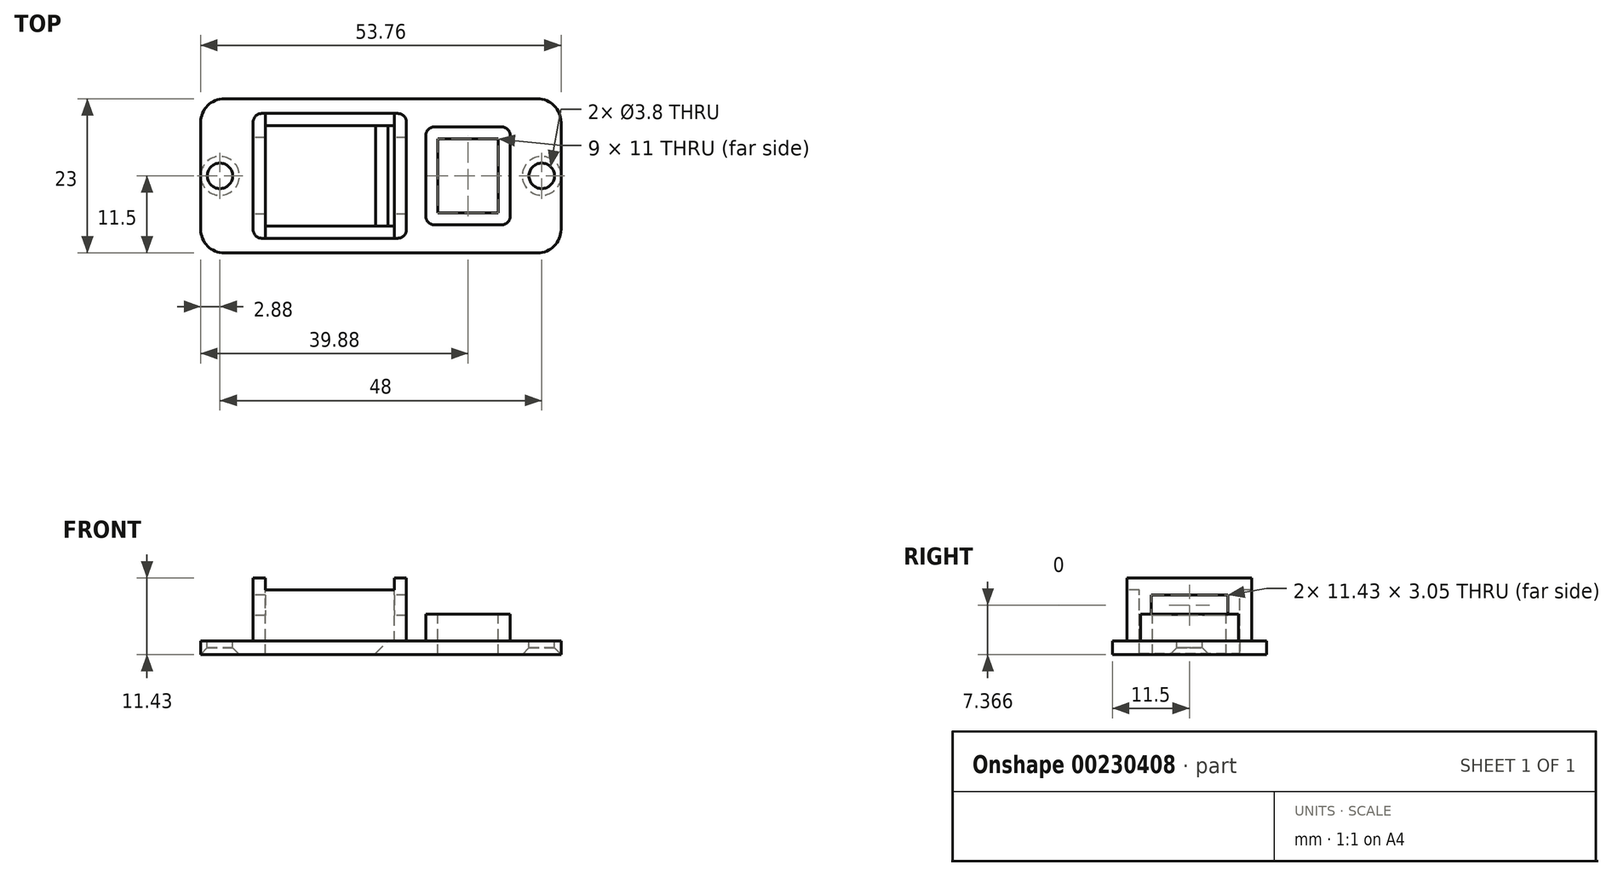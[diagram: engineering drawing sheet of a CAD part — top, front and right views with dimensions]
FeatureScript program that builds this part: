
annotation { "Feature Type Name" : "Feature", "Feature Type Description" : "" }
export const myFeature = defineFeature(function(context is Context, id is Id, definition is map)
    precondition{}
    {
        {
            var Q0;
            Q0=qCreatedBy(makeId("Top.planeOp"),FACE);
            var sketch = newSketch(context, id + "F0", { "sketchPlane" : qUnion([Q0])});
            skLineSegment(sketch, "E0.bottom", {"start": v(23.38, 11.5) * mm, "end": v(-23.38, 11.5) * mm});
            skLineSegment(sketch, "E0.top", {"start": v(23.37, -11.5) * mm, "end": v(-23.37, -11.5) * mm});
            skLineSegment(sketch, "E0.left", {"start": v(26.87, 8) * mm, "end": v(26.87, -8) * mm});
            skLineSegment(sketch, "E0.right", {"start": v(-26.88, 8) * mm, "end": v(-26.88, -8) * mm});
            skPoint(sketch, "E0.middle", {"position": v(0, 0) * mm});
            skPoint(sketch, "E1.visualSharp", {"position": v(-26.88, 11.5) * mm});
            skArc(sketch, "E1.filletArc", {"start": v(-23.38, 11.5) * mm, "mid": v(-25.85, 10.47) * mm, "end": v(-26.88, 8) * mm});
            skPoint(sketch, "E2.visualSharp", {"position": v(26.87, 11.5) * mm});
            skArc(sketch, "E2.filletArc", {"start": v(26.88, 8) * mm, "mid": v(25.85, 10.47) * mm, "end": v(23.38, 11.5) * mm});
            skPoint(sketch, "E3.visualSharp", {"position": v(26.87, -11.5) * mm});
            skArc(sketch, "E3.filletArc", {"start": v(23.38, -11.5) * mm, "mid": v(25.85, -10.47) * mm, "end": v(26.88, -8) * mm});
            skPoint(sketch, "E4.visualSharp", {"position": v(-26.87, -11.5) * mm});
            skArc(sketch, "E4.filletArc", {"start": v(-26.88, -8) * mm, "mid": v(-25.85, -10.47) * mm, "end": v(-23.38, -11.5) * mm});
            skSolve(sketch);
        }
        {
            var Q0;
            Q0=makeQuery(id+"F0.imprint","IMPRINT",FACE,{"disambiguationData":[TD([[makeQuery(id+"F0.imprint","IMPRINT",EDGE,{"derivedFrom":sQuery(id+"F0.wireOp",EDGE,"E0.bottom")}),1.0]])]});
            extrude(context, id + "F1", {"entities" : qUnion([Q0]), "depth" : 2 * mm});
        }
        {
            var Q0;
            Q0=makeQuery(id+"F1.opExtrude","CAP_FACE",FACE,{"disambiguationData":[OSD([sQuery(id+"F0.wireOp",EDGE,"E0.bottom"),sQuery(id+"F0.wireOp",EDGE,"E0.top"),sQuery(id+"F0.wireOp",EDGE,"E0.left"),sQuery(id+"F0.wireOp",EDGE,"E0.right"),sQuery(id+"F0.wireOp",EDGE,"E1.filletArc"),sQuery(id+"F0.wireOp",EDGE,"E2.filletArc"),sQuery(id+"F0.wireOp",EDGE,"E3.filletArc"),sQuery(id+"F0.wireOp",EDGE,"E4.filletArc")])],"isStart":false});
            var sketch = newSketch(context, id + "F2", { "sketchPlane" : qUnion([Q0])});
            skCircle(sketch, "E5", {"center": v(-24, 0) * mm, "radius": 1.9 * mm});
            skCircle(sketch, "E6", {"center": v(24, 0) * mm, "radius": 1.9 * mm});
            skSolve(sketch);
        }
        {
            var Q0;
            Q0 = qSketchRegion(id + "F2", true);
            extrude(context, id + "F3", {"entities" : qUnion([Q0]), "operationType" : NewBodyOperationType.REMOVE, "endBound" : BoundingType.THROUGH_ALL, "oppositeDirection" : true, "depth" : 25 * mm});
        }
        {
            var Q0;
            Q0=makeQuery(id+"F3.boolean.opBoolean","INTERSECT",EDGE,{"derivedFrom":[makeQuery(id+"F1.opExtrude","CAP_FACE",FACE,{"disambiguationData":[OSD([sQuery(id+"F0.wireOp",EDGE,"E0.bottom"),sQuery(id+"F0.wireOp",EDGE,"E0.top"),sQuery(id+"F0.wireOp",EDGE,"E0.left"),sQuery(id+"F0.wireOp",EDGE,"E0.right"),sQuery(id+"F0.wireOp",EDGE,"E1.filletArc"),sQuery(id+"F0.wireOp",EDGE,"E2.filletArc"),sQuery(id+"F0.wireOp",EDGE,"E3.filletArc"),sQuery(id+"F0.wireOp",EDGE,"E4.filletArc")])],"isStart":true}),makeQuery(id+"F3.opExtrude","SWEPT_FACE",FACE,{"disambiguationData":[OSD([sQuery(id+"F2.wireOp",EDGE,"E5")])]})]});
            var Q1;
            Q1=makeQuery(id+"F3.boolean.opBoolean","INTERSECT",EDGE,{"derivedFrom":[makeQuery(id+"F1.opExtrude","CAP_FACE",FACE,{"disambiguationData":[OSD([sQuery(id+"F0.wireOp",EDGE,"E0.bottom"),sQuery(id+"F0.wireOp",EDGE,"E0.top"),sQuery(id+"F0.wireOp",EDGE,"E0.left"),sQuery(id+"F0.wireOp",EDGE,"E0.right"),sQuery(id+"F0.wireOp",EDGE,"E1.filletArc"),sQuery(id+"F0.wireOp",EDGE,"E2.filletArc"),sQuery(id+"F0.wireOp",EDGE,"E3.filletArc"),sQuery(id+"F0.wireOp",EDGE,"E4.filletArc")])],"isStart":true}),makeQuery(id+"F3.opExtrude","SWEPT_FACE",FACE,{"disambiguationData":[OSD([sQuery(id+"F2.wireOp",EDGE,"E6")])]})]});
            chamfer(context, id + "F4", {"entities" : qUnion([Q0, Q1]), "width" : 1 * mm, "tangentPropagation" : true});
        }
        {
            var Q0;
            Q0=makeQuery(id+"F1.opExtrude","CAP_FACE",FACE,{"disambiguationData":[OSD([sQuery(id+"F0.wireOp",EDGE,"E0.bottom"),sQuery(id+"F0.wireOp",EDGE,"E0.top"),sQuery(id+"F0.wireOp",EDGE,"E0.left"),sQuery(id+"F0.wireOp",EDGE,"E0.right"),sQuery(id+"F0.wireOp",EDGE,"E1.filletArc"),sQuery(id+"F0.wireOp",EDGE,"E2.filletArc"),sQuery(id+"F0.wireOp",EDGE,"E3.filletArc"),sQuery(id+"F0.wireOp",EDGE,"E4.filletArc")])],"isStart":false});
            var sketch = newSketch(context, id + "F5", { "sketchPlane" : qUnion([Q0])});
            skLineSegment(sketch, "E7.bottom", {"start": v(2, -7.5) * mm, "end": v(-17.25, -7.5) * mm});
            skLineSegment(sketch, "E7.top", {"start": v(2, 7.5) * mm, "end": v(-17.25, 7.5) * mm});
            skLineSegment(sketch, "E7.left", {"start": v(2, -7.5) * mm, "end": v(2, 7.5) * mm});
            skLineSegment(sketch, "E7.right", {"start": v(-17.25, -7.5) * mm, "end": v(-17.25, 7.5) * mm});
            skPoint(sketch, "E7.middle", {"position": v(-7.63, 0) * mm});
            skSolve(sketch);
        }
        {
            var Q0;
            Q0 = qSketchRegion(id + "F5", true);
            extrude(context, id + "F6", {"entities" : qUnion([Q0]), "operationType" : NewBodyOperationType.REMOVE, "endBound" : BoundingType.THROUGH_ALL, "oppositeDirection" : true, "depth" : 25 * mm});
        }
        {
            var Q0;
            Q0=makeQuery(id+"F1.opExtrude","CAP_FACE",FACE,{"disambiguationData":[OSD([sQuery(id+"F0.wireOp",EDGE,"E0.bottom"),sQuery(id+"F0.wireOp",EDGE,"E0.top"),sQuery(id+"F0.wireOp",EDGE,"E0.left"),sQuery(id+"F0.wireOp",EDGE,"E0.right"),sQuery(id+"F0.wireOp",EDGE,"E1.filletArc"),sQuery(id+"F0.wireOp",EDGE,"E2.filletArc"),sQuery(id+"F0.wireOp",EDGE,"E3.filletArc"),sQuery(id+"F0.wireOp",EDGE,"E4.filletArc")])],"isStart":false});
            var sketch = newSketch(context, id + "F7", { "sketchPlane" : qUnion([Q0])});
            skLineSegment(sketch, "E8.0", {"start": v(2, 7.5) * mm, "end": v(-17.25, 7.5) * mm});
            skLineSegment(sketch, "E9.0", {"start": v(-17.25, -7.5) * mm, "end": v(-17.25, 7.5) * mm});
            skLineSegment(sketch, "E10.0", {"start": v(2, -7.5) * mm, "end": v(-17.25, -7.5) * mm});
            skLineSegment(sketch, "E11.0", {"start": v(2, -7.5) * mm, "end": v(2, 7.5) * mm});
            skLineSegment(sketch, "E12.0", {"start": v(2.53, 9.3) * mm, "end": v(-17.78, 9.3) * mm});
            skLineSegment(sketch, "E12.1", {"start": v(3.8, -8.04) * mm, "end": v(3.8, 8.04) * mm});
            skLineSegment(sketch, "E12.2", {"start": v(2.53, -9.3) * mm, "end": v(-17.78, -9.3) * mm});
            skLineSegment(sketch, "E12.3", {"start": v(-19.05, -8.04) * mm, "end": v(-19.05, 8.04) * mm});
            skPoint(sketch, "E13.visualSharp", {"position": v(-19.05, 9.3) * mm});
            skArc(sketch, "E13.filletArc", {"start": v(-17.78, 9.3) * mm, "mid": v(-18.68, 8.93) * mm, "end": v(-19.05, 8.04) * mm});
            skPoint(sketch, "E14.visualSharp", {"position": v(3.8, 9.3) * mm});
            skArc(sketch, "E14.filletArc", {"start": v(3.8, 8.04) * mm, "mid": v(3.43, 8.93) * mm, "end": v(2.53, 9.3) * mm});
            skPoint(sketch, "E15.visualSharp", {"position": v(3.8, -9.3) * mm});
            skArc(sketch, "E15.filletArc", {"start": v(2.53, -9.3) * mm, "mid": v(3.43, -8.93) * mm, "end": v(3.8, -8.04) * mm});
            skPoint(sketch, "E16.visualSharp", {"position": v(-19.05, -9.3) * mm});
            skArc(sketch, "E16.filletArc", {"start": v(-19.05, -8.04) * mm, "mid": v(-18.68, -8.93) * mm, "end": v(-17.78, -9.3) * mm});
            skSolve(sketch);
        }
        {
            var Q0;
            Q0 = qSketchRegion(id + "F7", true);
            extrude(context, id + "F8", {"entities" : qUnion([Q0]), "operationType" : NewBodyOperationType.ADD, "depth" : 11.43 * mm - 2 * mm});
        }
        {
            var Q0;
            Q0=makeQuery(id+"F8.opExtrude","SWEPT_FACE",FACE,{"disambiguationData":[OSD([sQuery(id+"F7.wireOp",EDGE,"E12.3")])]});
            var sketch = newSketch(context, id + "F9", { "sketchPlane" : qUnion([Q0])});
            skLineSegment(sketch, "E17.bottom", {"start": v(5.71, 5.84) * mm, "end": v(-5.72, 5.84) * mm});
            skLineSegment(sketch, "E17.top", {"start": v(5.71, 8.9) * mm, "end": v(-5.72, 8.9) * mm});
            skLineSegment(sketch, "E17.left", {"start": v(5.71, 5.84) * mm, "end": v(5.71, 8.9) * mm});
            skLineSegment(sketch, "E17.right", {"start": v(-5.72, 5.84) * mm, "end": v(-5.72, 8.89) * mm});
            skPoint(sketch, "E17.middle", {"position": v(0, 7.37) * mm});
            skSolve(sketch);
        }
        {
            var Q0;
            Q0 = qSketchRegion(id + "F9", true);
            extrude(context, id + "F10", {"entities" : qUnion([Q0]), "operationType" : NewBodyOperationType.REMOVE, "endBound" : BoundingType.THROUGH_ALL, "oppositeDirection" : true, "depth" : 25 * mm});
        }
        {
            var Q0;
            Q0=makeQuery(id+"F8.opExtrude","CAP_FACE",FACE,{"disambiguationData":[OSD([sQuery(id+"F7.wireOp",EDGE,"E8.0"),sQuery(id+"F7.wireOp",EDGE,"E9.0"),sQuery(id+"F7.wireOp",EDGE,"E10.0"),sQuery(id+"F7.wireOp",EDGE,"E11.0"),sQuery(id+"F7.wireOp",EDGE,"E12.0"),sQuery(id+"F7.wireOp",EDGE,"E12.1"),sQuery(id+"F7.wireOp",EDGE,"E12.2"),sQuery(id+"F7.wireOp",EDGE,"E12.3"),sQuery(id+"F7.wireOp",EDGE,"E13.filletArc"),sQuery(id+"F7.wireOp",EDGE,"E14.filletArc"),sQuery(id+"F7.wireOp",EDGE,"E15.filletArc"),sQuery(id+"F7.wireOp",EDGE,"E16.filletArc")])],"isStart":false});
            var sketch = newSketch(context, id + "F11", { "sketchPlane" : qUnion([Q0])});
            skLineSegment(sketch, "E18.bottom", {"start": v(2, 9.3) * mm, "end": v(-17.25, 9.3) * mm});
            skLineSegment(sketch, "E18.top", {"start": v(2, -9.3) * mm, "end": v(-17.25, -9.3) * mm});
            skLineSegment(sketch, "E18.left", {"start": v(2, 9.3) * mm, "end": v(2, -9.3) * mm});
            skLineSegment(sketch, "E18.right", {"start": v(-17.25, 9.3) * mm, "end": v(-17.25, -9.3) * mm});
            skSolve(sketch);
        }
        {
            var Q0;
            Q0 = qSketchRegion(id + "F11", true);
            extrude(context, id + "F12", {"entities" : qUnion([Q0]), "operationType" : NewBodyOperationType.REMOVE, "oppositeDirection" : true, "depth" : 1.78 * mm});
        }
        {
            var Q0;
            Q0=makeQuery(id+"F1.opExtrude","CAP_FACE",FACE,{"disambiguationData":[OSD([sQuery(id+"F0.wireOp",EDGE,"E0.bottom"),sQuery(id+"F0.wireOp",EDGE,"E0.top"),sQuery(id+"F0.wireOp",EDGE,"E0.left"),sQuery(id+"F0.wireOp",EDGE,"E0.right"),sQuery(id+"F0.wireOp",EDGE,"E1.filletArc"),sQuery(id+"F0.wireOp",EDGE,"E2.filletArc"),sQuery(id+"F0.wireOp",EDGE,"E3.filletArc"),sQuery(id+"F0.wireOp",EDGE,"E4.filletArc")])],"isStart":true});
            var sketch = newSketch(context, id + "F13", { "sketchPlane" : qUnion([Q0])});
            skLineSegment(sketch, "E19.bottom", {"start": v(2, -7.5) * mm, "end": v(-0.75, -7.5) * mm});
            skLineSegment(sketch, "E19.top", {"start": v(2, 7.5) * mm, "end": v(-0.75, 7.5) * mm});
            skLineSegment(sketch, "E19.left", {"start": v(2, -7.5) * mm, "end": v(2, 7.5) * mm});
            skLineSegment(sketch, "E19.right", {"start": v(-0.75, -7.5) * mm, "end": v(-0.75, 7.5) * mm});
            skSolve(sketch);
        }
        {
            var Q0;
            Q0 = qSketchRegion(id + "F13", true);
            extrude(context, id + "F14", {"entities" : qUnion([Q0]), "operationType" : NewBodyOperationType.ADD, "oppositeDirection" : true, "depth" : 2 * mm});
        }
        {
            var Q0;
            Q0=makeQuery(id+"F14.opExtrude","CAP_EDGE",EDGE,{"disambiguationData":[OSD([sQuery(id+"F13.wireOp",EDGE,"E19.right")])],"isStart":false});
            chamfer(context, id + "F15", {"entities" : qUnion([Q0]), "width" : 1.8 * mm, "tangentPropagation" : true});
        }
        {
            var Q0;
            Q0=makeQuery(id+"F1.opExtrude","CAP_FACE",FACE,{"disambiguationData":[OSD([sQuery(id+"F0.wireOp",EDGE,"E0.bottom"),sQuery(id+"F0.wireOp",EDGE,"E0.top"),sQuery(id+"F0.wireOp",EDGE,"E0.left"),sQuery(id+"F0.wireOp",EDGE,"E0.right"),sQuery(id+"F0.wireOp",EDGE,"E1.filletArc"),sQuery(id+"F0.wireOp",EDGE,"E2.filletArc"),sQuery(id+"F0.wireOp",EDGE,"E3.filletArc"),sQuery(id+"F0.wireOp",EDGE,"E4.filletArc")])],"isStart":false});
            var sketch = newSketch(context, id + "F16", { "sketchPlane" : qUnion([Q0])});
            skLineSegment(sketch, "E20.bottom", {"start": v(8.5, -5.5) * mm, "end": v(17.5, -5.5) * mm});
            skLineSegment(sketch, "E20.top", {"start": v(8.5, 5.5) * mm, "end": v(17.5, 5.5) * mm});
            skLineSegment(sketch, "E20.left", {"start": v(8.5, -5.5) * mm, "end": v(8.5, 5.5) * mm});
            skLineSegment(sketch, "E20.right", {"start": v(17.5, -5.5) * mm, "end": v(17.5, 5.5) * mm});
            skPoint(sketch, "E20.middle", {"position": v(13, 0) * mm});
            skSolve(sketch);
        }
        {
            var Q0;
            Q0 = qSketchRegion(id + "F16", true);
            extrude(context, id + "F17", {"entities" : qUnion([Q0]), "operationType" : NewBodyOperationType.REMOVE, "endBound" : BoundingType.THROUGH_ALL, "oppositeDirection" : true, "depth" : 25 * mm});
        }
        {
            var Q0;
            Q0=makeQuery(id+"F1.opExtrude","CAP_FACE",FACE,{"disambiguationData":[OSD([sQuery(id+"F0.wireOp",EDGE,"E0.bottom"),sQuery(id+"F0.wireOp",EDGE,"E0.top"),sQuery(id+"F0.wireOp",EDGE,"E0.left"),sQuery(id+"F0.wireOp",EDGE,"E0.right"),sQuery(id+"F0.wireOp",EDGE,"E1.filletArc"),sQuery(id+"F0.wireOp",EDGE,"E2.filletArc"),sQuery(id+"F0.wireOp",EDGE,"E3.filletArc"),sQuery(id+"F0.wireOp",EDGE,"E4.filletArc")])],"isStart":false});
            var sketch = newSketch(context, id + "F18", { "sketchPlane" : qUnion([Q0])});
            skLineSegment(sketch, "E21.0", {"start": v(17.5, -5.5) * mm, "end": v(17.5, 5.5) * mm});
            skLineSegment(sketch, "E22.0", {"start": v(8.5, 5.5) * mm, "end": v(17.5, 5.5) * mm});
            skLineSegment(sketch, "E23.0", {"start": v(8.5, -5.5) * mm, "end": v(8.5, 5.5) * mm});
            skLineSegment(sketch, "E24.0", {"start": v(8.5, -5.5) * mm, "end": v(17.5, -5.5) * mm});
            skLineSegment(sketch, "E25.0", {"start": v(19.3, -6.03) * mm, "end": v(19.3, 6.03) * mm});
            skLineSegment(sketch, "E25.1", {"start": v(7.97, -7.3) * mm, "end": v(18.03, -7.3) * mm});
            skLineSegment(sketch, "E25.2", {"start": v(6.7, -6.03) * mm, "end": v(6.7, 6.03) * mm});
            skLineSegment(sketch, "E25.3", {"start": v(7.97, 7.3) * mm, "end": v(18.03, 7.3) * mm});
            skPoint(sketch, "E26.visualSharp", {"position": v(19.3, 7.3) * mm});
            skArc(sketch, "E26.filletArc", {"start": v(19.3, 6.03) * mm, "mid": v(18.93, 6.93) * mm, "end": v(18.03, 7.3) * mm});
            skPoint(sketch, "E27.visualSharp", {"position": v(19.3, -7.3) * mm});
            skArc(sketch, "E27.filletArc", {"start": v(18.03, -7.3) * mm, "mid": v(18.93, -6.93) * mm, "end": v(19.3, -6.03) * mm});
            skPoint(sketch, "E28.visualSharp", {"position": v(6.7, -7.3) * mm});
            skArc(sketch, "E28.filletArc", {"start": v(6.7, -6.03) * mm, "mid": v(7.07, -6.93) * mm, "end": v(7.97, -7.3) * mm});
            skPoint(sketch, "E29.visualSharp", {"position": v(6.7, 7.3) * mm});
            skArc(sketch, "E29.filletArc", {"start": v(7.97, 7.3) * mm, "mid": v(7.07, 6.93) * mm, "end": v(6.7, 6.03) * mm});
            skSolve(sketch);
        }
        {
            var Q0;
            Q0 = qSketchRegion(id + "F18", true);
            extrude(context, id + "F19", {"entities" : qUnion([Q0]), "operationType" : NewBodyOperationType.ADD, "depth" : 4 * mm});
        }
    });
